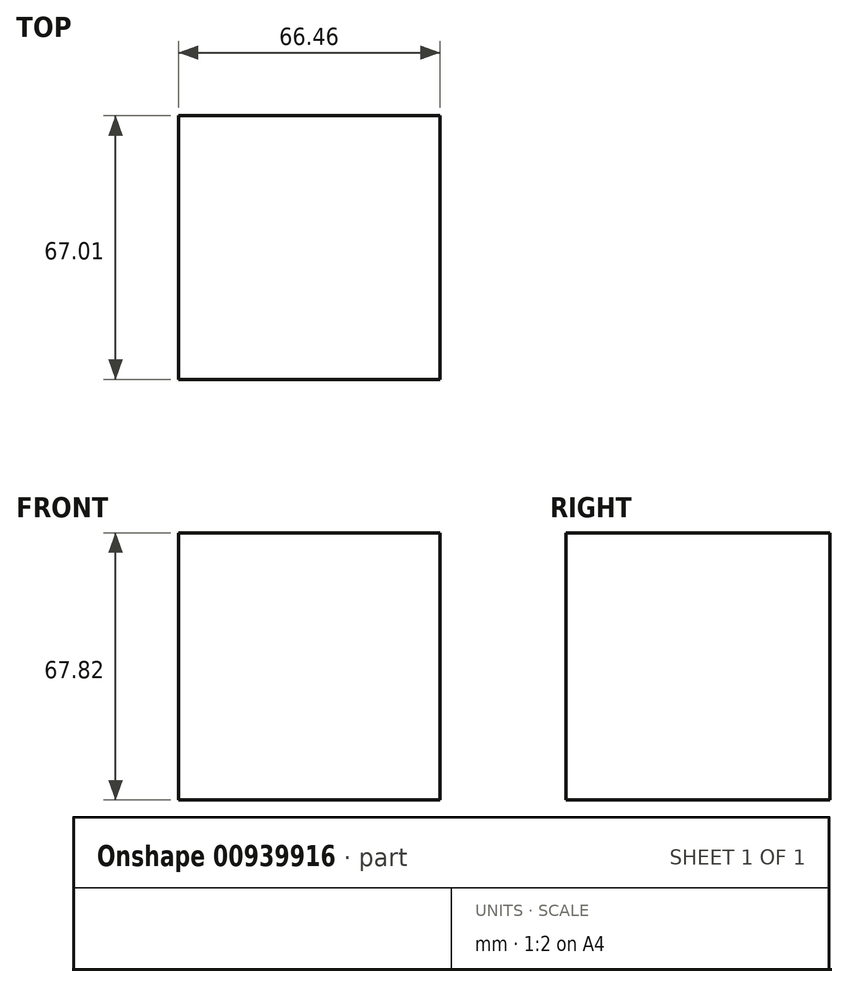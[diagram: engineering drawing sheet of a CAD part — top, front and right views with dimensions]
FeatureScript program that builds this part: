
annotation { "Feature Type Name" : "Feature", "Feature Type Description" : "" }
export const myFeature = defineFeature(function(context is Context, id is Id, definition is map)
    precondition{}
    {
        {
            var Q0;
            Q0=qCreatedBy(makeId("Top.planeOp"),FACE);
            var sketch = newSketch(context, id + "F0", { "sketchPlane" : qUnion([Q0])});
            skLineSegment(sketch, "E0.bottom", {"start": v(0, 0) * mm, "end": v(-66.46, 0) * mm});
            skLineSegment(sketch, "E0.top", {"start": v(0, 67.01) * mm, "end": v(-66.46, 67.01) * mm});
            skLineSegment(sketch, "E0.left", {"start": v(0, 0) * mm, "end": v(0, 67.01) * mm});
            skLineSegment(sketch, "E0.right", {"start": v(-66.46, 0) * mm, "end": v(-66.46, 67.01) * mm});
            skSolve(sketch);
        }
        {
            var Q0;
            Q0=makeQuery(id+"F0.imprint","IMPRINT",FACE,{"disambiguationData":[TD([[makeQuery(id+"F0.imprint","IMPRINT",EDGE,{"derivedFrom":sQuery(id+"F0.wireOp",EDGE,"E0.bottom")}),-1.0]])]});
            extrude(context, id + "F1", {"entities" : qUnion([Q0]), "depth" : 67.82 * mm, "offsetDistance" : 25.4 * mm});
        }
    });
